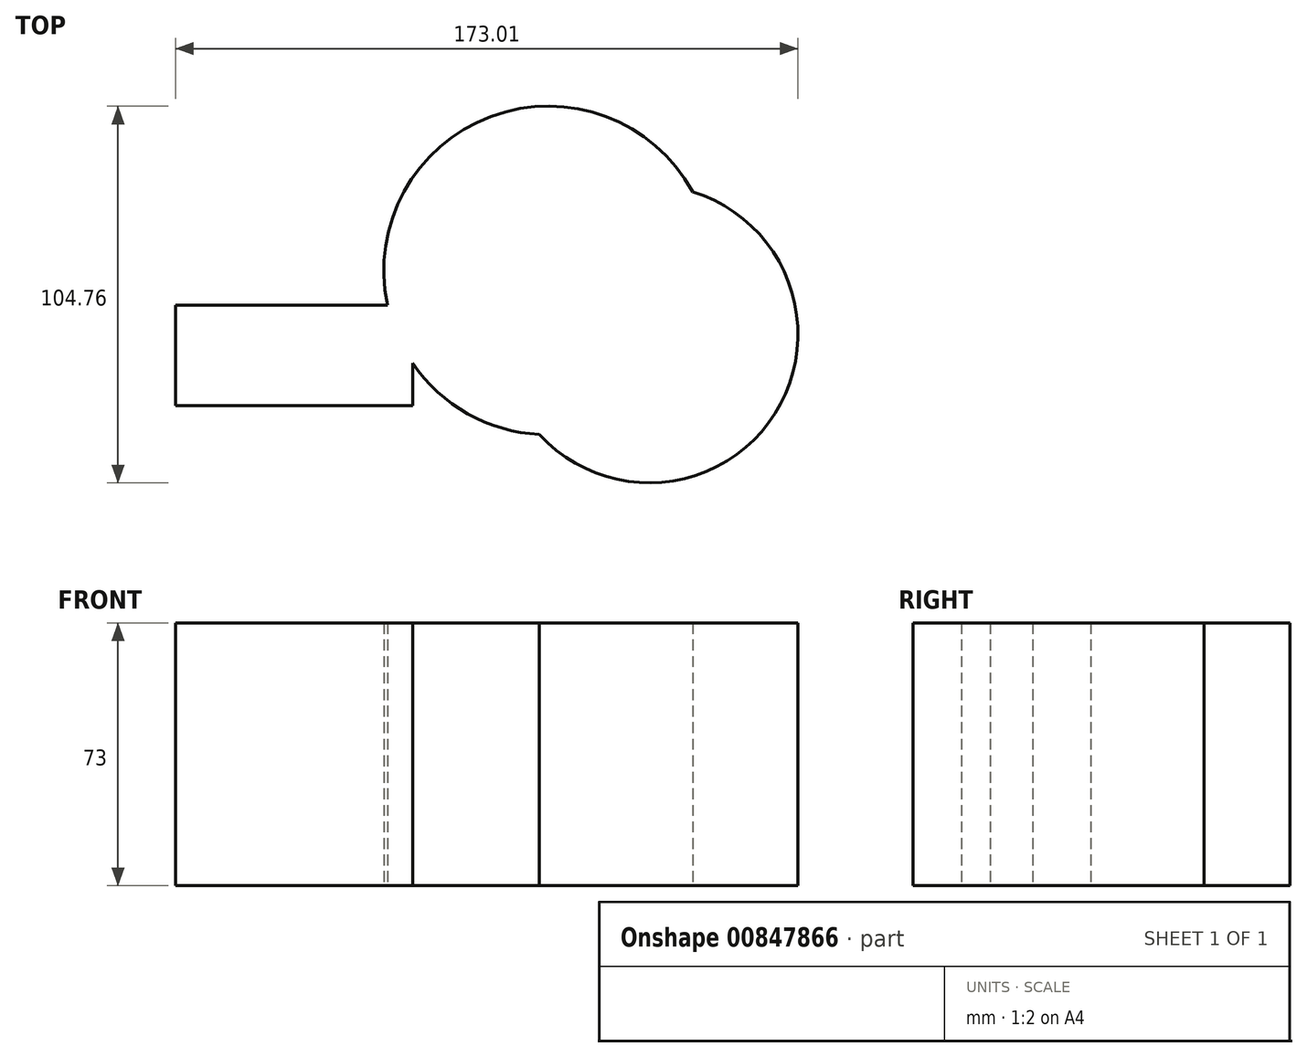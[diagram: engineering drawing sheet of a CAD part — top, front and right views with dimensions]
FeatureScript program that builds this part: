
annotation { "Feature Type Name" : "Feature", "Feature Type Description" : "" }
export const myFeature = defineFeature(function(context is Context, id is Id, definition is map)
    precondition{}
    {
        {
            var Q0;
            Q0=qCreatedBy(makeId("Top.planeOp"),FACE);
            var sketch = newSketch(context, id + "F0", { "sketchPlane" : qUnion([Q0])});
            skLineSegment(sketch, "E0.bottom", {"start": v(-131.65, 8.07) * mm, "end": v(-65.75, 8.07) * mm});
            skLineSegment(sketch, "E0.top", {"start": v(-131.65, -19.92) * mm, "end": v(-65.75, -19.92) * mm});
            skLineSegment(sketch, "E0.left", {"start": v(-131.65, 8.07) * mm, "end": v(-131.65, -19.92) * mm});
            skLineSegment(sketch, "E0.right", {"start": v(-65.75, 8.07) * mm, "end": v(-65.75, -19.92) * mm});
            skCircle(sketch, "E1", {"center": v(-28.05, 17.7) * mm, "radius": 45.7 * mm});
            skCircle(sketch, "E2", {"center": v(0, 0) * mm, "radius": 41.36 * mm});
            skSolve(sketch);
        }
        {
            var Q0;
            Q0 = qSketchRegion(id + "F0", true);
            extrude(context, id + "F1", {"entities" : qUnion([Q0]), "depth" : 73 * mm, "offsetDistance" : 25 * mm});
        }
    });
